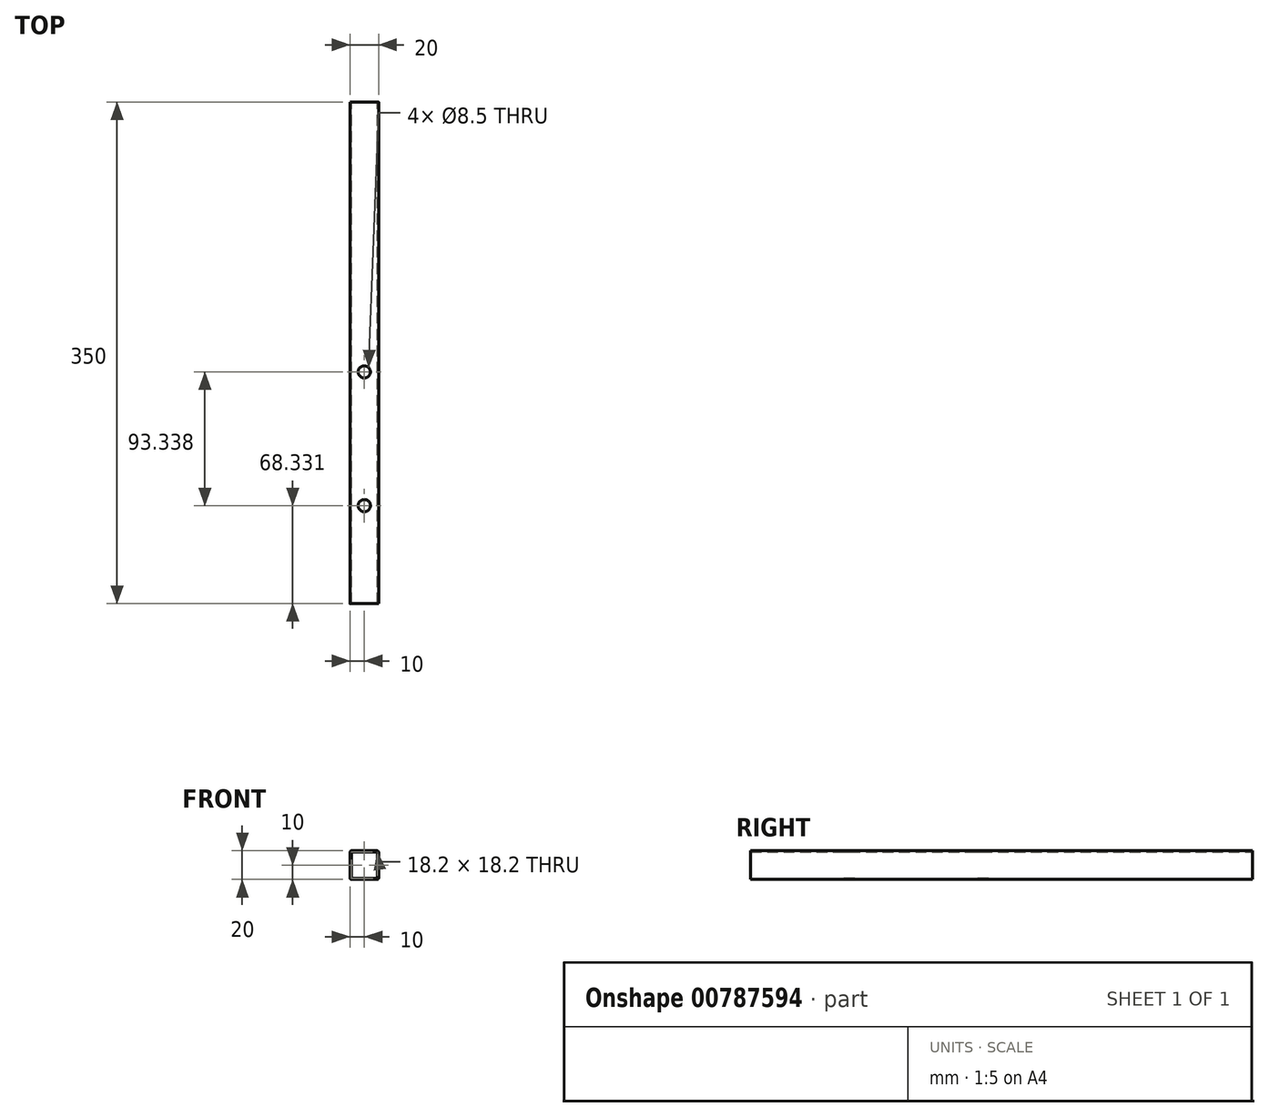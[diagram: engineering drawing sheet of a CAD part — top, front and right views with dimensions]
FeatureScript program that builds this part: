
annotation { "Feature Type Name" : "Feature", "Feature Type Description" : "" }
export const myFeature = defineFeature(function(context is Context, id is Id, definition is map)
    precondition{}
    {
        {
            var Q0;
            Q0=qCreatedBy(makeId("Front.planeOp"),FACE);
            var sketch = newSketch(context, id + "F0", { "sketchPlane" : qUnion([Q0])});
            skLineSegment(sketch, "E0.bottom", {"start": v(-10, 10) * mm, "end": v(10, 10) * mm});
            skLineSegment(sketch, "E0.top", {"start": v(-10, -10) * mm, "end": v(10, -10) * mm});
            skLineSegment(sketch, "E0.left", {"start": v(-10, 10) * mm, "end": v(-10, -10) * mm});
            skLineSegment(sketch, "E0.right", {"start": v(10, 10) * mm, "end": v(10, -10) * mm});
            skPoint(sketch, "E0.middle", {"position": v(0, 0) * mm});
            skLineSegment(sketch, "E1.0", {"start": v(-9.1, 9.1) * mm, "end": v(9.1, 9.1) * mm});
            skLineSegment(sketch, "E1.1", {"start": v(-9.1, 9.1) * mm, "end": v(-9.1, -9.1) * mm});
            skLineSegment(sketch, "E1.2", {"start": v(-9.1, -9.1) * mm, "end": v(9.1, -9.1) * mm});
            skLineSegment(sketch, "E1.3", {"start": v(9.1, 9.1) * mm, "end": v(9.1, -9.1) * mm});
            skSolve(sketch);
        }
        {
            var Q0;
            Q0=makeQuery(id+"F0.imprint","IMPRINT",FACE,{"disambiguationData":[TD([[makeQuery(id+"F0.imprint","IMPRINT",EDGE,{"derivedFrom":sQuery(id+"F0.wireOp",EDGE,"E0.bottom")}),-1.0]])]});
            extrude(context, id + "F1", {"entities" : qUnion([Q0]), "endBound" : BoundingType.SYMMETRIC, "depth" : 350 * mm, "offsetDistance" : 25 * mm});
        }
        {
            var Q0;
            Q0=makeQuery(id+"F1.opExtrude","SWEPT_EDGE",EDGE,{"disambiguationData":[OSD([sQuery(id+"F0.wireOp",EDGE,"E0.bottom"),sQuery(id+"F0.wireOp",EDGE,"E0.right")])]});
            var Q1;
            Q1=makeQuery(id+"F1.opExtrude","SWEPT_EDGE",EDGE,{"disambiguationData":[OSD([sQuery(id+"F0.wireOp",EDGE,"E0.bottom"),sQuery(id+"F0.wireOp",EDGE,"E0.left")])]});
            var Q2;
            Q2=makeQuery(id+"F1.opExtrude","SWEPT_EDGE",EDGE,{"disambiguationData":[OSD([sQuery(id+"F0.wireOp",EDGE,"E0.top"),sQuery(id+"F0.wireOp",EDGE,"E0.right")])]});
            var Q3;
            Q3=makeQuery(id+"F1.opExtrude","SWEPT_EDGE",EDGE,{"disambiguationData":[OSD([sQuery(id+"F0.wireOp",EDGE,"E0.top"),sQuery(id+"F0.wireOp",EDGE,"E0.left")])]});
            fillet(context, id + "F2", {"entities" : qUnion([Q0, Q1, Q2, Q3]), "radius" : 1 * mm, "tangentPropagation" : true, "allowEdgeOverflow" : false});
        }
        {
            var Q0;
            Q0=makeQuery(id+"F1.opExtrude","SWEPT_FACE",FACE,{"disambiguationData":[OSD([sQuery(id+"F0.wireOp",EDGE,"E0.bottom")])]});
            var sketch = newSketch(context, id + "F3", { "sketchPlane" : qUnion([Q0])});
            skLineSegment(sketch, "E2", {"start": v(0, -175) * mm, "end": v(0, -60) * mm});
            skPoint(sketch, "E3", {"position": v(0, -106.67) * mm});
            skPoint(sketch, "E4", {"position": v(0, -13.33) * mm});
            skSolve(sketch);
        }
        {
            var Q0;
            Q0=sQuery(id+"F3.wireOp",VERTEX,"E4");
            var Q1;
            Q1=sQuery(id+"F3.wireOp",VERTEX,"E3");
            var Q2;
            Q2=makeQuery(id+"F1.opExtrude","SWEPT_BODY",BODY,{"disambiguationData":[OSD([sQuery(id+"F0.wireOp",EDGE,"E0.bottom"),sQuery(id+"F0.wireOp",EDGE,"E0.top"),sQuery(id+"F0.wireOp",EDGE,"E0.left"),sQuery(id+"F0.wireOp",EDGE,"E0.right"),sQuery(id+"F0.wireOp",EDGE,"E1.0"),sQuery(id+"F0.wireOp",EDGE,"E1.1"),sQuery(id+"F0.wireOp",EDGE,"E1.2"),sQuery(id+"F0.wireOp",EDGE,"E1.3")])]});
            hole(context, id + "F4", {"style" : HoleStyle.SIMPLE, "endStyle" : HoleEndStyle.THROUGH, "holeDiameter" : 8.5 * mm, "majorDiameter" : 5 * mm, "isTappedThrough" : true, "tappedDepth" : 12 * mm, "tapClearance" : 3, "locations" : qUnion([Q0, Q1]), "scope" : qUnion([Q2])});
        }
    });
